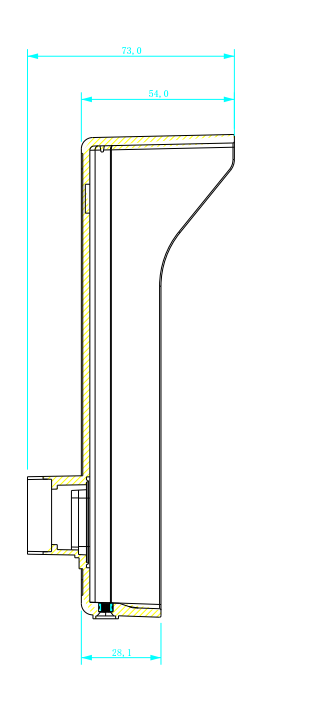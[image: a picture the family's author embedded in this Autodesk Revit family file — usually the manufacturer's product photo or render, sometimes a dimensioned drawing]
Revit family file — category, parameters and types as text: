
# Revit family: SH-42
name_source: partatom
category: Устройства связи
units: mm (PartAtom-declared; Revit-internal decimal feet)

## family parameters
Всегда вертикально = Нет
На основе рабочей плоскости = Да
Общий = Да
При загрузке вырезать с полостями = Нет
Размер круглого соединителя = Использовать диаметр
Сохранять ориентацию аннотаций = Нет
Тип детали = Нормальный
Точка принадлежности помещению = Нет

## types (1)
- SH-42
    ADSK_Версия Revit = Revit 2020
    ADSK_Единица измерения = шт
    ADSK_Завод-изготовитель = BAS-IP
    ADSK_Классификация нагрузок = Модуль управления двумя замками
    ADSK_Количество фаз = 1
    ADSK_Коэффициент мощности = 0.9
    ADSK_Марка = SH-42
    ADSK_Наименование = Модуль управления двумя замками SH-42
    ADSK_Наименование краткое = SH-42
    ADSK_Напряжение = 12 В
    ADSK_Номинальная мощность = 0 Вт
    ADSK_Полная мощность = 1 В·А
    ADSK_Размер_Длина = 115 мм
    ADSK_Размер_Толщина = 34 мм
    ADSK_Размер_Ширина = 58 мм
    BIM library = https://bimlib.ru
    Product Documentation Link = https://www.bas-ip.com.ua
    Product Page URL = https://www.bas-ip.com.ua
    URL = https://www.bas-ip.ru
    Габаритные размеры = 114,5×57,5×34 мм
    Группа модели = Модуль управления двумя замками SH-42
    Допустимая влажность = 20 – 80 %
    Изготовитель = BAS-IP
    Изображение типоразмера = <Нет>
    Максимальное переменное напряжение нагрузки = ~250 В
    Максимальное постоянное напряжение нагрузки = +30 В
    Максимальный ток подключаемой нагрузки = 7 А (на каждый канал)
    Масса = 0,11 кг
    Материал корпуса = Материал белый
    Мощность потребления в рабочем режиме = 1 Вт
    Мощность потребления в режиме ожидания = 0,06 Вт
    Напряжение питания модуля = +12 В
    Описание = Модуль управления двумя замками SH-42 - Модуль управления предназначен для подключения двух замков и управления ими с внутреннего монитора. Подключение модуля к вызывной панели производится посредством 485 интерфейса между модулем и вызывной панелью. Работает со всеми панелями за исключением AV-02
    Отметка по умолчанию = 0 мм
    Степень защиты = IP30C
    Температура хранения = -15 – +65 °C
    Температура эксплуатации = -40 – +75 °C
